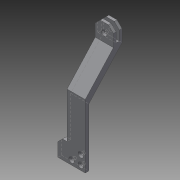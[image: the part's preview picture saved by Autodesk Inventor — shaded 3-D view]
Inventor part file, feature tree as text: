
AUTODESK INVENTOR PART (.ipt)
format: ipt  version: 2015 (Build 190159000, 159)  size: 187,392 bytes
history: native  units: mm
features: sketch x10, extrude x8, hole x2, chamfer x2
ambient origin geometry x8: Origin, YZ Plane, XZ Plane, XY Plane, X Axis, Y Axis, Z Axis, Center Point
bodies: Solid1 (feature_tree)
feature tree (22):
  extrude  "Extrusion1"  Depth=4.0mm
  extrude  "Extrusion2"  Depth=103.0mm
  hole  "Hole1"  [1 undecoded]
  chamfer  "Chamfer1"  Distance=5.0mm Angle=45.0deg
  extrude  "Extrusion3"  Depth=20.0mm TaperAngle=0.0deg
  extrude  "Extrusion4"  Depth=4.0mm
  extrude  "Extrusion5"  Depth=30.0mm
  extrude  "Extrusion6"  Depth=20.0mm TaperAngle=0.0deg
  extrude  "Extrusion7"  Depth=3.0mm
  extrude  "Extrusion8"  Depth=3.0mm
  hole  "Hole2"  [1 undecoded]
  chamfer  "Chamfer2"  Distance=3.0mm
  sketch  "Sketch1"  dims[d0=30.0mm d1=4.0mm]
  sketch  "Sketch2"  dims[d2=20.0mm d3=0.0mm d4=103.0mm]
  sketch  "Sketch3"  dims[d5=20.0mm d6=10.0mm d7=0.0mm]
  sketch  "Sketch4"  dims[d8=5.0mm]
  sketch  "Sketch5"  dims[d9=5.0mm]
  sketch  "Sketch6"  dims[d10=5.0mm]
  sketch  "Sketch7"  dims[d11=5.0mm]
  sketch  "Sketch8"  dims[d12=5.0mm]
  sketch  "Sketch9"  dims[d13=10.0mm]
  sketch  "Sketch10"  dims[d14=3.0mm d15=6.0mm d16=6.0mm d17=2.0mm d18=90.0deg d19=8.0mm d20=20.594885mm d21=5.0mm d22=2.0mm d23=45.0deg d24=20.0mm d25=0.0mm d26=4.0mm d27=30.0mm d28=20.0mm d29=0.0mm d30=15.0mm d31=3.0mm d32=3.5mm d33=3.0mm d34=4.0mm d35=20.0mm d36=0.0mm d37=1.0mm d38=20.0mm d39=0.0mm d40=50.0mm d41=20.0mm d42=0.0mm d43=20.0mm d44=0.0mm d45=6.0mm d46=3.0mm d47=6.0mm d48=6.0mm d49=2.0mm d50=90.0deg d51=15.0mm d52=20.594885mm d53=5.5mm d54=2.0mm d55=45.0deg]
note: 2 required parameter values undecoded (feature->parameter linkage not recoverable at this tier; creation-order binding heuristic only, values carry confidence <= 0.55)
